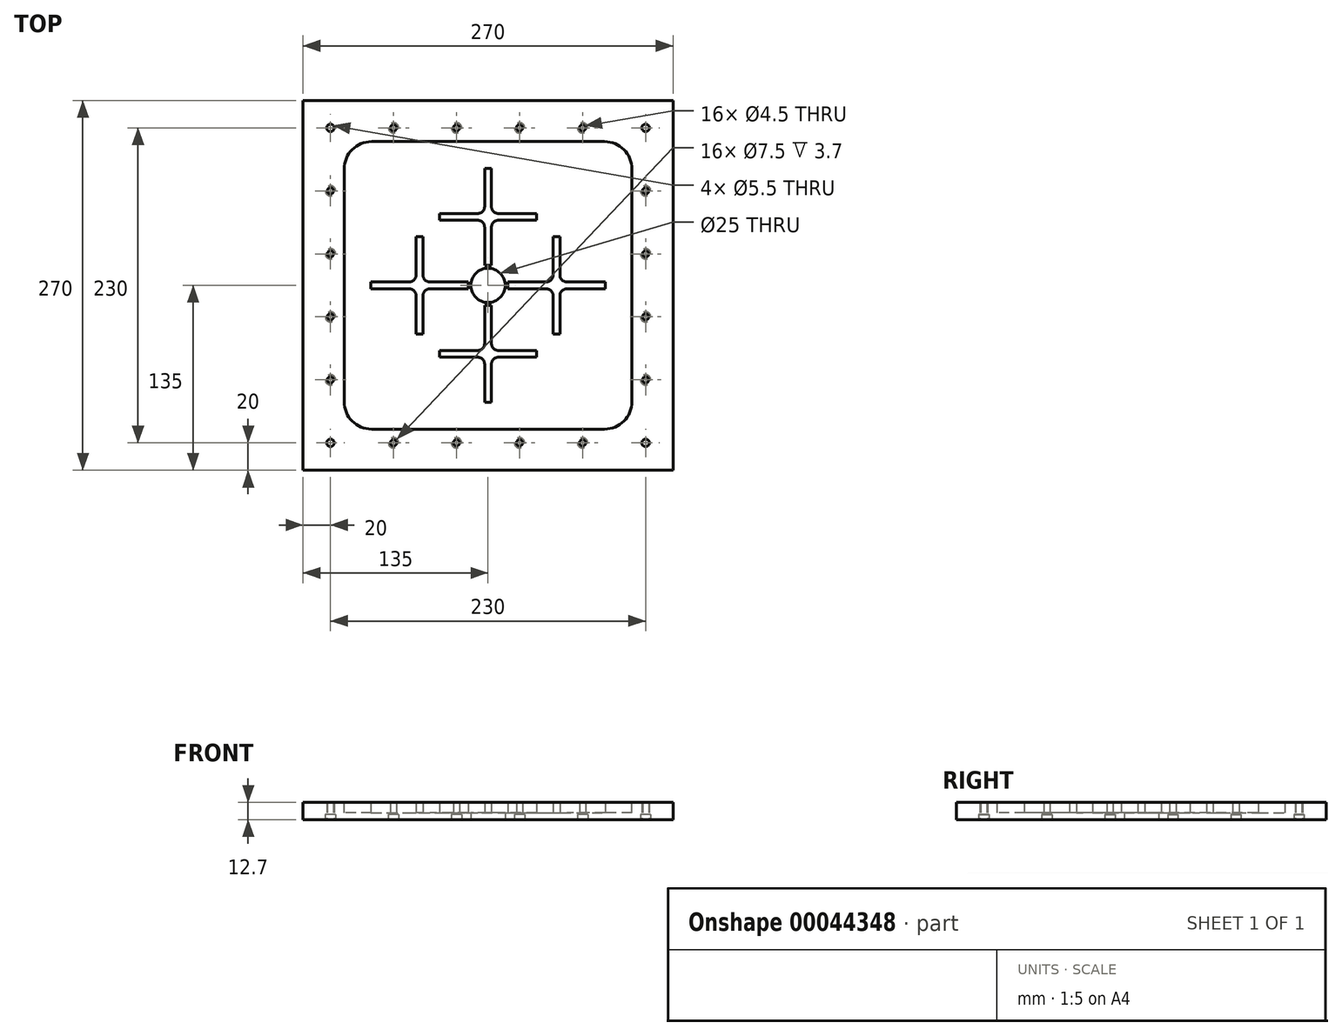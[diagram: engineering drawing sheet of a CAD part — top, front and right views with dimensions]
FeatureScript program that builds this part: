
annotation { "Feature Type Name" : "Feature", "Feature Type Description" : "" }
export const myFeature = defineFeature(function(context is Context, id is Id, definition is map)
    precondition{}
    {
        {
            var Q0;
            Q0=qCreatedBy(makeId("Top.planeOp"),FACE);
            var sketch = newSketch(context, id + "F0", { "sketchPlane" : qUnion([Q0])});
            skLineSegment(sketch, "E0.bottom", {"start": v(0, 0) * mm, "end": v(270, 0) * mm});
            skLineSegment(sketch, "E0.top", {"start": v(0, 270) * mm, "end": v(270, 270) * mm});
            skLineSegment(sketch, "E0.left", {"start": v(0, 0) * mm, "end": v(0, 270) * mm});
            skLineSegment(sketch, "E0.right", {"start": v(270, 0) * mm, "end": v(270, 270) * mm});
            skCircle(sketch, "E1", {"center": v(135, 135) * mm, "radius": 12.5 * mm});
            skCircle(sketch, "E2", {"center": v(20, 250) * mm, "radius": 2.75 * mm});
            skCircle(sketch, "E3", {"center": v(250, 250) * mm, "radius": 2.75 * mm});
            skCircle(sketch, "E4", {"center": v(20, 20) * mm, "radius": 2.75 * mm});
            skCircle(sketch, "E5", {"center": v(250, 20) * mm, "radius": 2.75 * mm});
            skCircle(sketch, "E6", {"center": v(66, 20) * mm, "radius": 2.25 * mm});
            skCircle(sketch, "E7.1.0.0", {"center": v(112, 20) * mm, "radius": 2.25 * mm});
            skCircle(sketch, "E7.2.0.0", {"center": v(158, 20) * mm, "radius": 2.25 * mm});
            skCircle(sketch, "E7.3.0.0", {"center": v(204, 20) * mm, "radius": 2.25 * mm});
            skLineSegment(sketch, "E7.direction1", {"start": v(66, 20) * mm, "end": v(112, 20) * mm, "construction": true});
            skCircle(sketch, "E8", {"center": v(20, 66) * mm, "radius": 2.25 * mm});
            skCircle(sketch, "E9.0.1.0", {"center": v(20, 112) * mm, "radius": 2.25 * mm});
            skCircle(sketch, "E9.0.2.0", {"center": v(20, 158) * mm, "radius": 2.25 * mm});
            skCircle(sketch, "E9.0.3.0", {"center": v(20, 204) * mm, "radius": 2.25 * mm});
            skLineSegment(sketch, "E9.direction1", {"start": v(20, 66) * mm, "end": v(45, 66) * mm, "construction": true});
            skLineSegment(sketch, "E9.direction2", {"start": v(20, 66) * mm, "end": v(20, 112) * mm, "construction": true});
            skCircle(sketch, "E10", {"center": v(66, 250) * mm, "radius": 2.25 * mm});
            skCircle(sketch, "E11.1.0.1", {"center": v(112, 250) * mm, "radius": 2.25 * mm});
            skCircle(sketch, "E11.2.0.1", {"center": v(158, 250) * mm, "radius": 2.25 * mm});
            skCircle(sketch, "E11.3.0.1", {"center": v(204, 250) * mm, "radius": 2.25 * mm});
            skLineSegment(sketch, "E11.direction1", {"start": v(66, 250) * mm, "end": v(112, 250) * mm, "construction": true});
            skCircle(sketch, "E12", {"center": v(250, 66) * mm, "radius": 2.25 * mm});
            skCircle(sketch, "E13.0.1.0", {"center": v(250, 112) * mm, "radius": 2.25 * mm});
            skCircle(sketch, "E13.0.2.0", {"center": v(250, 158) * mm, "radius": 2.25 * mm});
            skCircle(sketch, "E13.0.3.0", {"center": v(250, 204) * mm, "radius": 2.25 * mm});
            skLineSegment(sketch, "E13.direction1", {"start": v(250, 66) * mm, "end": v(275, 66) * mm, "construction": true});
            skLineSegment(sketch, "E13.direction2", {"start": v(250, 66) * mm, "end": v(250, 112) * mm, "construction": true});
            skSolve(sketch);
        }
        {
            var Q0;
            Q0=makeQuery(id+"F0.imprint","IMPRINT",FACE,{"disambiguationData":[TD([[makeQuery(id+"F0.imprint","IMPRINT",EDGE,{"derivedFrom":sQuery(id+"F0.wireOp",EDGE,"E0.bottom")}),1.0]])]});
            extrude(context, id + "F1", {"entities" : qUnion([Q0]), "depth" : 12.7 * mm});
        }
        {
            var Q0;
            Q0=makeQuery(id+"F0.imprint","IMPRINT",FACE,{"disambiguationData":[TD([[makeQuery(id+"F0.imprint","IMPRINT",EDGE,{"derivedFrom":sQuery(id+"F0.wireOp",EDGE,"E0.bottom")}),1.0]])]});
            var sketch = newSketch(context, id + "F2", { "sketchPlane" : qUnion([Q0])});
            skCircle(sketch, "E14", {"center": v(66, 20) * mm, "radius": 3.75 * mm});
            skCircle(sketch, "E15.1.0.0", {"center": v(112, 20) * mm, "radius": 3.75 * mm});
            skCircle(sketch, "E15.2.0.0", {"center": v(158, 20) * mm, "radius": 3.75 * mm});
            skCircle(sketch, "E15.3.0.0", {"center": v(204, 20) * mm, "radius": 3.75 * mm});
            skLineSegment(sketch, "E15.direction1", {"start": v(66, 20) * mm, "end": v(112, 20) * mm, "construction": true});
            skCircle(sketch, "E16", {"center": v(20, 66) * mm, "radius": 3.75 * mm});
            skCircle(sketch, "E17.0.1.0", {"center": v(20, 112) * mm, "radius": 3.75 * mm});
            skCircle(sketch, "E17.0.2.0", {"center": v(20, 158) * mm, "radius": 3.75 * mm});
            skCircle(sketch, "E17.0.3.0", {"center": v(20, 204) * mm, "radius": 3.75 * mm});
            skLineSegment(sketch, "E17.direction1", {"start": v(20, 66) * mm, "end": v(45, 66) * mm, "construction": true});
            skLineSegment(sketch, "E17.direction2", {"start": v(20, 66) * mm, "end": v(20, 112) * mm, "construction": true});
            skCircle(sketch, "E18", {"center": v(250, 66) * mm, "radius": 3.75 * mm});
            skCircle(sketch, "E19.0.1.0", {"center": v(250, 112) * mm, "radius": 3.75 * mm});
            skCircle(sketch, "E19.0.2.0", {"center": v(250, 158) * mm, "radius": 3.75 * mm});
            skCircle(sketch, "E19.0.3.0", {"center": v(250, 204) * mm, "radius": 3.75 * mm});
            skLineSegment(sketch, "E19.direction1", {"start": v(250, 66) * mm, "end": v(275, 66) * mm, "construction": true});
            skLineSegment(sketch, "E19.direction2", {"start": v(250, 66) * mm, "end": v(250, 112) * mm, "construction": true});
            skCircle(sketch, "E20", {"center": v(66, 250) * mm, "radius": 3.75 * mm});
            skCircle(sketch, "E21.1.0.0", {"center": v(112, 250) * mm, "radius": 3.75 * mm});
            skCircle(sketch, "E21.2.0.0", {"center": v(158, 250) * mm, "radius": 3.75 * mm});
            skCircle(sketch, "E21.3.0.0", {"center": v(204, 250) * mm, "radius": 3.75 * mm});
            skLineSegment(sketch, "E21.direction1", {"start": v(66, 250) * mm, "end": v(112, 250) * mm, "construction": true});
            skSolve(sketch);
        }
        {
            var Q0;
            Q0=makeQuery(id+"F2.imprint","IMPRINT",FACE,{"disambiguationData":[TD([[makeQuery(id+"F2.imprint","IMPRINT",EDGE,{"derivedFrom":sQuery(id+"F2.wireOp",EDGE,"E17.0.3.0")}),1.0]])]});
            var Q1;
            Q1=makeQuery(id+"F2.imprint","IMPRINT",FACE,{"disambiguationData":[TD([[makeQuery(id+"F2.imprint","IMPRINT",EDGE,{"derivedFrom":sQuery(id+"F2.wireOp",EDGE,"E20")}),1.0]])]});
            var Q2;
            Q2=makeQuery(id+"F2.imprint","IMPRINT",FACE,{"disambiguationData":[TD([[makeQuery(id+"F2.imprint","IMPRINT",EDGE,{"derivedFrom":sQuery(id+"F2.wireOp",EDGE,"E17.0.2.0")}),1.0]])]});
            var Q3;
            Q3=makeQuery(id+"F2.imprint","IMPRINT",FACE,{"disambiguationData":[TD([[makeQuery(id+"F2.imprint","IMPRINT",EDGE,{"derivedFrom":sQuery(id+"F2.wireOp",EDGE,"E17.0.1.0")}),1.0]])]});
            var Q4;
            Q4=makeQuery(id+"F2.imprint","IMPRINT",FACE,{"disambiguationData":[TD([[makeQuery(id+"F2.imprint","IMPRINT",EDGE,{"derivedFrom":sQuery(id+"F2.wireOp",EDGE,"E16")}),1.0]])]});
            var Q5;
            Q5=makeQuery(id+"F2.imprint","IMPRINT",FACE,{"disambiguationData":[TD([[makeQuery(id+"F2.imprint","IMPRINT",EDGE,{"derivedFrom":sQuery(id+"F2.wireOp",EDGE,"E14")}),1.0]])]});
            var Q6;
            Q6=makeQuery(id+"F2.imprint","IMPRINT",FACE,{"disambiguationData":[TD([[makeQuery(id+"F2.imprint","IMPRINT",EDGE,{"derivedFrom":sQuery(id+"F2.wireOp",EDGE,"E15.1.0.0")}),1.0]])]});
            var Q7;
            Q7=makeQuery(id+"F2.imprint","IMPRINT",FACE,{"disambiguationData":[TD([[makeQuery(id+"F2.imprint","IMPRINT",EDGE,{"derivedFrom":sQuery(id+"F2.wireOp",EDGE,"E15.2.0.0")}),1.0]])]});
            var Q8;
            Q8=makeQuery(id+"F2.imprint","IMPRINT",FACE,{"disambiguationData":[TD([[makeQuery(id+"F2.imprint","IMPRINT",EDGE,{"derivedFrom":sQuery(id+"F2.wireOp",EDGE,"E15.3.0.0")}),1.0]])]});
            var Q9;
            Q9=makeQuery(id+"F2.imprint","IMPRINT",FACE,{"disambiguationData":[TD([[makeQuery(id+"F2.imprint","IMPRINT",EDGE,{"derivedFrom":sQuery(id+"F2.wireOp",EDGE,"E18")}),1.0]])]});
            var Q10;
            Q10=makeQuery(id+"F2.imprint","IMPRINT",FACE,{"disambiguationData":[TD([[makeQuery(id+"F2.imprint","IMPRINT",EDGE,{"derivedFrom":sQuery(id+"F2.wireOp",EDGE,"E19.0.1.0")}),1.0]])]});
            var Q11;
            Q11=makeQuery(id+"F2.imprint","IMPRINT",FACE,{"disambiguationData":[TD([[makeQuery(id+"F2.imprint","IMPRINT",EDGE,{"derivedFrom":sQuery(id+"F2.wireOp",EDGE,"E19.0.2.0")}),1.0]])]});
            var Q12;
            Q12=makeQuery(id+"F2.imprint","IMPRINT",FACE,{"disambiguationData":[TD([[makeQuery(id+"F2.imprint","IMPRINT",EDGE,{"derivedFrom":sQuery(id+"F2.wireOp",EDGE,"E19.0.3.0")}),1.0]])]});
            var Q13;
            Q13=makeQuery(id+"F2.imprint","IMPRINT",FACE,{"disambiguationData":[TD([[makeQuery(id+"F2.imprint","IMPRINT",EDGE,{"derivedFrom":sQuery(id+"F2.wireOp",EDGE,"E21.1.0.0")}),1.0]])]});
            var Q14;
            Q14=makeQuery(id+"F2.imprint","IMPRINT",FACE,{"disambiguationData":[TD([[makeQuery(id+"F2.imprint","IMPRINT",EDGE,{"derivedFrom":sQuery(id+"F2.wireOp",EDGE,"E21.2.0.0")}),1.0]])]});
            var Q15;
            Q15=makeQuery(id+"F2.imprint","IMPRINT",FACE,{"disambiguationData":[TD([[makeQuery(id+"F2.imprint","IMPRINT",EDGE,{"derivedFrom":sQuery(id+"F2.wireOp",EDGE,"E21.3.0.0")}),1.0]])]});
            extrude(context, id + "F3", {"entities" : qUnion([Q0, Q1, Q2, Q3, Q4, Q5, Q6, Q7, Q8, Q9, Q10, Q11, Q12, Q13, Q14, Q15]), "operationType" : NewBodyOperationType.REMOVE, "depth" : 3.7 * mm});
        }
        {
            var Q0;
            Q0=makeQuery(id+"F1.opExtrude","CAP_FACE",FACE,{"disambiguationData":[OSD([sQuery(id+"F0.wireOp",EDGE,"E0.bottom"),sQuery(id+"F0.wireOp",EDGE,"E0.top"),sQuery(id+"F0.wireOp",EDGE,"E0.left"),sQuery(id+"F0.wireOp",EDGE,"E0.right"),sQuery(id+"F0.wireOp",EDGE,"E1"),sQuery(id+"F0.wireOp",EDGE,"E2"),sQuery(id+"F0.wireOp",EDGE,"E3"),sQuery(id+"F0.wireOp",EDGE,"E4"),sQuery(id+"F0.wireOp",EDGE,"E5"),sQuery(id+"F0.wireOp",EDGE,"E6"),sQuery(id+"F0.wireOp",EDGE,"E7.1.0.0"),sQuery(id+"F0.wireOp",EDGE,"E7.2.0.0"),sQuery(id+"F0.wireOp",EDGE,"E7.3.0.0"),sQuery(id+"F0.wireOp",EDGE,"E8"),sQuery(id+"F0.wireOp",EDGE,"E9.0.1.0"),sQuery(id+"F0.wireOp",EDGE,"E9.0.2.0"),sQuery(id+"F0.wireOp",EDGE,"E9.0.3.0"),sQuery(id+"F0.wireOp",EDGE,"E10"),sQuery(id+"F0.wireOp",EDGE,"E11.1.0.1"),sQuery(id+"F0.wireOp",EDGE,"E11.2.0.1"),sQuery(id+"F0.wireOp",EDGE,"E11.3.0.1"),sQuery(id+"F0.wireOp",EDGE,"E12"),sQuery(id+"F0.wireOp",EDGE,"E13.0.1.0"),sQuery(id+"F0.wireOp",EDGE,"E13.0.2.0"),sQuery(id+"F0.wireOp",EDGE,"E13.0.3.0")])],"isStart":false});
            var sketch = newSketch(context, id + "F4", { "sketchPlane" : qUnion([Q0])});
            skLineSegment(sketch, "E22.bottom", {"start": v(50, 240) * mm, "end": v(220, 240) * mm});
            skLineSegment(sketch, "E22.top", {"start": v(50, 30) * mm, "end": v(220, 30) * mm});
            skLineSegment(sketch, "E22.left", {"start": v(30, 220) * mm, "end": v(30, 50) * mm});
            skLineSegment(sketch, "E22.right", {"start": v(240, 220) * mm, "end": v(240, 50) * mm});
            skPoint(sketch, "E23.visualSharp", {"position": v(30, 240) * mm});
            skArc(sketch, "E23.filletArc", {"start": v(50, 240) * mm, "mid": v(35.86, 234.14) * mm, "end": v(30, 220) * mm});
            skPoint(sketch, "E24.visualSharp", {"position": v(240, 240) * mm});
            skArc(sketch, "E24.filletArc", {"start": v(240, 220) * mm, "mid": v(234.14, 234.14) * mm, "end": v(220, 240) * mm});
            skPoint(sketch, "E25.visualSharp", {"position": v(240, 30) * mm});
            skArc(sketch, "E25.filletArc", {"start": v(220, 30) * mm, "mid": v(234.14, 35.86) * mm, "end": v(240, 50) * mm});
            skPoint(sketch, "E26.visualSharp", {"position": v(30, 30) * mm});
            skArc(sketch, "E26.filletArc", {"start": v(30, 50) * mm, "mid": v(35.86, 35.86) * mm, "end": v(50, 30) * mm});
            skSolve(sketch);
        }
        {
            var Q0;
            Q0=makeQuery(id+"F4.imprint","IMPRINT",FACE,{"disambiguationData":[TD([[makeQuery(id+"F4.imprint","IMPRINT",EDGE,{"derivedFrom":sQuery(id+"F4.wireOp",EDGE,"E22.bottom")}),-1.0]])]});
            extrude(context, id + "F5", {"entities" : qUnion([Q0]), "operationType" : NewBodyOperationType.REMOVE, "oppositeDirection" : true, "depth" : 7.7 * mm});
        }
        {
            var Q0;
            Q0=makeQuery(id+"F2.imprint","IMPRINT",FACE,{"disambiguationData":[TD([[makeQuery(id+"F2.imprint","IMPRINT",EDGE,{"derivedFrom":sQuery(id+"F2.wireOp",EDGE,"E14")}),-1.0]])]});
            var sketch = newSketch(context, id + "F6", { "sketchPlane" : qUnion([Q0])});
            skLineSegment(sketch, "E27.0", {"start": v(82.5, 170.5) * mm, "end": v(82.5, 142.5) * mm});
            skLineSegment(sketch, "E28.0", {"start": v(87.5, 170.5) * mm, "end": v(87.5, 142.5) * mm});
            skLineSegment(sketch, "E29", {"start": v(82.5, 170.5) * mm, "end": v(87.5, 170.5) * mm});
            skLineSegment(sketch, "E30", {"start": v(92.5, 137.5) * mm, "end": v(120.5, 137.5) * mm});
            skLineSegment(sketch, "E31.0", {"start": v(92.5, 132.5) * mm, "end": v(120.5, 132.5) * mm});
            skLineSegment(sketch, "E32", {"start": v(120.5, 137.5) * mm, "end": v(120.5, 132.5) * mm});
            skLineSegment(sketch, "E33", {"start": v(87.5, 127.5) * mm, "end": v(87.5, 99.5) * mm});
            skLineSegment(sketch, "E34.0", {"start": v(82.5, 127.5) * mm, "end": v(82.5, 99.5) * mm});
            skLineSegment(sketch, "E35", {"start": v(87.5, 99.5) * mm, "end": v(82.5, 99.5) * mm});
            skLineSegment(sketch, "E36", {"start": v(77.5, 132.5) * mm, "end": v(49.5, 132.5) * mm});
            skLineSegment(sketch, "E37.0", {"start": v(77.5, 137.5) * mm, "end": v(49.5, 137.5) * mm});
            skLineSegment(sketch, "E38", {"start": v(49.5, 137.5) * mm, "end": v(49.5, 132.5) * mm});
            skPoint(sketch, "E39.visualSharp", {"position": v(82.5, 137.5) * mm});
            skArc(sketch, "E39.filletArc", {"start": v(77.5, 137.5) * mm, "mid": v(81.04, 138.96) * mm, "end": v(82.5, 142.5) * mm});
            skPoint(sketch, "E40.visualSharp", {"position": v(87.5, 137.5) * mm});
            skArc(sketch, "E40.filletArc", {"start": v(87.5, 142.5) * mm, "mid": v(88.96, 138.96) * mm, "end": v(92.5, 137.5) * mm});
            skPoint(sketch, "E41.visualSharp", {"position": v(82.5, 132.5) * mm});
            skArc(sketch, "E41.filletArc", {"start": v(82.5, 127.5) * mm, "mid": v(81.04, 131.04) * mm, "end": v(77.5, 132.5) * mm});
            skPoint(sketch, "E42.visualSharp", {"position": v(87.5, 132.5) * mm});
            skArc(sketch, "E42.filletArc", {"start": v(92.5, 132.5) * mm, "mid": v(88.96, 131.04) * mm, "end": v(87.5, 127.5) * mm});
            skArc(sketch, "E43.MirrorCS", {"start": v(182.5, 142.5) * mm, "mid": v(181.04, 138.96) * mm, "end": v(177.5, 137.5) * mm});
            skArc(sketch, "E44.MirrorCS", {"start": v(177.5, 132.5) * mm, "mid": v(181.04, 131.04) * mm, "end": v(182.5, 127.5) * mm});
            skArc(sketch, "E45.MirrorCS", {"start": v(187.5, 127.5) * mm, "mid": v(188.96, 131.04) * mm, "end": v(192.5, 132.5) * mm});
            skArc(sketch, "E46.MirrorCS", {"start": v(192.5, 137.5) * mm, "mid": v(188.96, 138.96) * mm, "end": v(187.5, 142.5) * mm});
            skLineSegment(sketch, "E47.MirrorCS", {"start": v(220.5, 137.5) * mm, "end": v(220.5, 132.5) * mm});
            skLineSegment(sketch, "E48.MirrorCS", {"start": v(149.5, 137.5) * mm, "end": v(149.5, 132.5) * mm});
            skLineSegment(sketch, "E49.MirrorCS", {"start": v(182.5, 99.5) * mm, "end": v(187.5, 99.5) * mm});
            skLineSegment(sketch, "E50.MirrorCS", {"start": v(187.5, 170.5) * mm, "end": v(182.5, 170.5) * mm});
            skPoint(sketch, "E51.MirrorP", {"position": v(187.5, 137.5) * mm});
            skPoint(sketch, "E52.MirrorP", {"position": v(182.5, 132.5) * mm});
            skPoint(sketch, "E53.MirrorP", {"position": v(187.5, 132.5) * mm});
            skLineSegment(sketch, "E54.MirrorCS", {"start": v(192.5, 137.5) * mm, "end": v(220.5, 137.5) * mm});
            skLineSegment(sketch, "E55.MirrorCS", {"start": v(187.5, 170.5) * mm, "end": v(187.5, 142.5) * mm});
            skLineSegment(sketch, "E56.MirrorCS", {"start": v(187.5, 127.5) * mm, "end": v(187.5, 99.5) * mm});
            skLineSegment(sketch, "E57.MirrorCS", {"start": v(182.5, 127.5) * mm, "end": v(182.5, 99.5) * mm});
            skLineSegment(sketch, "E58.MirrorCS", {"start": v(177.5, 132.5) * mm, "end": v(149.5, 132.5) * mm});
            skLineSegment(sketch, "E59.MirrorCS", {"start": v(177.5, 137.5) * mm, "end": v(149.5, 137.5) * mm});
            skPoint(sketch, "E60.MirrorP", {"position": v(182.5, 137.5) * mm});
            skLineSegment(sketch, "E61.MirrorCS", {"start": v(182.5, 170.5) * mm, "end": v(182.5, 142.5) * mm});
            skLineSegment(sketch, "E62.MirrorCS", {"start": v(192.5, 132.5) * mm, "end": v(220.5, 132.5) * mm});
            skLineSegment(sketch, "E63.0", {"start": v(137.5, 220.5) * mm, "end": v(137.5, 192.5) * mm});
            skLineSegment(sketch, "E64", {"start": v(127.5, 182.5) * mm, "end": v(99.5, 182.5) * mm});
            skPoint(sketch, "E65.visualSharp", {"position": v(132.5, 182.5) * mm});
            skLineSegment(sketch, "E66.0", {"start": v(142.5, 182.5) * mm, "end": v(170.5, 182.5) * mm});
            skLineSegment(sketch, "E67", {"start": v(137.5, 177.5) * mm, "end": v(137.5, 149.5) * mm});
            skLineSegment(sketch, "E68.0", {"start": v(132.5, 220.5) * mm, "end": v(132.5, 192.5) * mm});
            skLineSegment(sketch, "E69.0", {"start": v(132.5, 177.5) * mm, "end": v(132.5, 149.5) * mm});
            skPoint(sketch, "E70.visualSharp", {"position": v(137.5, 187.5) * mm});
            skLineSegment(sketch, "E71", {"start": v(142.5, 187.5) * mm, "end": v(170.5, 187.5) * mm});
            skLineSegment(sketch, "E72.0", {"start": v(127.5, 187.5) * mm, "end": v(99.5, 187.5) * mm});
            skPoint(sketch, "E73.visualSharp", {"position": v(132.5, 187.5) * mm});
            skPoint(sketch, "E74.visualSharp", {"position": v(137.5, 182.5) * mm});
            skArc(sketch, "E65.filletArc", {"start": v(132.5, 177.5) * mm, "mid": v(131.04, 181.04) * mm, "end": v(127.5, 182.5) * mm});
            skLineSegment(sketch, "E75", {"start": v(132.5, 220.5) * mm, "end": v(137.5, 220.5) * mm});
            skLineSegment(sketch, "E76", {"start": v(170.5, 187.5) * mm, "end": v(170.5, 182.5) * mm});
            skLineSegment(sketch, "E77", {"start": v(137.5, 149.5) * mm, "end": v(132.5, 149.5) * mm});
            skArc(sketch, "E74.filletArc", {"start": v(142.5, 182.5) * mm, "mid": v(138.96, 181.04) * mm, "end": v(137.5, 177.5) * mm});
            skArc(sketch, "E70.filletArc", {"start": v(137.5, 192.5) * mm, "mid": v(138.96, 188.96) * mm, "end": v(142.5, 187.5) * mm});
            skLineSegment(sketch, "E78", {"start": v(99.5, 187.5) * mm, "end": v(99.5, 182.5) * mm});
            skArc(sketch, "E73.filletArc", {"start": v(127.5, 187.5) * mm, "mid": v(131.04, 188.96) * mm, "end": v(132.5, 192.5) * mm});
            skLineSegment(sketch, "E79.MirrorCS", {"start": v(132.5, 49.5) * mm, "end": v(137.5, 49.5) * mm});
            skLineSegment(sketch, "E80.MirrorCS", {"start": v(99.5, 82.5) * mm, "end": v(99.5, 87.5) * mm});
            skArc(sketch, "E81.MirrorCS", {"start": v(137.5, 77.5) * mm, "mid": v(138.96, 81.04) * mm, "end": v(142.5, 82.5) * mm});
            skLineSegment(sketch, "E82.MirrorCS", {"start": v(137.5, 120.5) * mm, "end": v(132.5, 120.5) * mm});
            skLineSegment(sketch, "E83.MirrorCS", {"start": v(170.5, 82.5) * mm, "end": v(170.5, 87.5) * mm});
            skArc(sketch, "E84.MirrorCS", {"start": v(142.5, 87.5) * mm, "mid": v(138.96, 88.96) * mm, "end": v(137.5, 92.5) * mm});
            skArc(sketch, "E85.MirrorCS", {"start": v(132.5, 92.5) * mm, "mid": v(131.04, 88.96) * mm, "end": v(127.5, 87.5) * mm});
            skPoint(sketch, "E86.MirrorP", {"position": v(137.5, 82.5) * mm});
            skArc(sketch, "E87.MirrorCS", {"start": v(127.5, 82.5) * mm, "mid": v(131.04, 81.04) * mm, "end": v(132.5, 77.5) * mm});
            skLineSegment(sketch, "E88.MirrorCS", {"start": v(142.5, 87.5) * mm, "end": v(170.5, 87.5) * mm});
            skLineSegment(sketch, "E89.MirrorCS", {"start": v(132.5, 49.5) * mm, "end": v(132.5, 77.5) * mm});
            skLineSegment(sketch, "E90.MirrorCS", {"start": v(137.5, 49.5) * mm, "end": v(137.5, 77.5) * mm});
            skPoint(sketch, "E91.MirrorP", {"position": v(132.5, 87.5) * mm});
            skLineSegment(sketch, "E92.MirrorCS", {"start": v(137.5, 92.5) * mm, "end": v(137.5, 120.5) * mm});
            skLineSegment(sketch, "E93.MirrorCS", {"start": v(132.5, 92.5) * mm, "end": v(132.5, 120.5) * mm});
            skLineSegment(sketch, "E94.MirrorCS", {"start": v(142.5, 82.5) * mm, "end": v(170.5, 82.5) * mm});
            skLineSegment(sketch, "E95.MirrorCS", {"start": v(127.5, 82.5) * mm, "end": v(99.5, 82.5) * mm});
            skLineSegment(sketch, "E96.MirrorCS", {"start": v(127.5, 87.5) * mm, "end": v(99.5, 87.5) * mm});
            skPoint(sketch, "E97.MirrorP", {"position": v(132.5, 82.5) * mm});
            skPoint(sketch, "E98.MirrorP", {"position": v(137.5, 87.5) * mm});
            skSolve(sketch);
        }
        {
            var Q0;
            Q0 = qSketchRegion(id + "F6", true);
            extrude(context, id + "F7", {"entities" : qUnion([Q0]), "operationType" : NewBodyOperationType.ADD, "depth" : 12.7 * mm});
        }
    });
